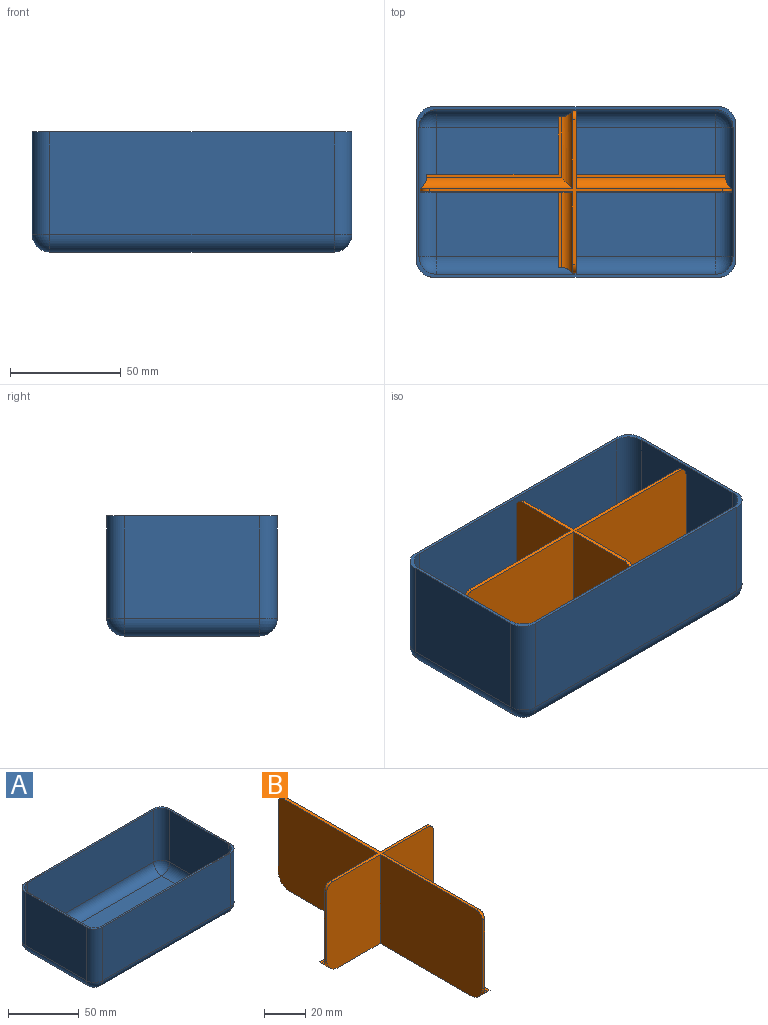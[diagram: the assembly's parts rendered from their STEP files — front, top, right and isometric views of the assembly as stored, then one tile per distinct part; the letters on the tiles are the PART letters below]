
ASSEMBLY  parts=2 mates=1
PART A: 35 faces, bbox 144.6x77.1x54.3 mm
  f0: plane 61.1x46.3mm, normal (1,0,0), area 2828.9mm2, adj f8,f13,f16,f26
  f1: plane 128.6x46.3mm, normal (0,1,0), area 5954.2mm2, adj f8,f13,f14,f22
  f2: plane 61.1x46.3mm, normal (-1,0,0), area 2828.9mm2, adj f8,f14,f15,f19
  f3: plane 58.5x45mm, normal (1,0,0), area 2632.5mm2, adj f8,f9,f12,f32
  f4: plane 126x45mm, normal (0,-1,0), area 5670mm2, adj f8,f9,f10,f28
  f5: plane 58.5x45mm, normal (-1,0,0), area 2632.5mm2, adj f8,f10,f11,f29
  f6: plane 126x45mm, normal (0,1,0), area 5670mm2, adj f8,f11,f12,f33
  f7: plane 128.6x46.3mm, normal (0,-1,0), area 5954.2mm2, adj f8,f15,f16,f23
  f8: plane 144.6x77.1mm, normal (0,0,1), area 569.7mm2, adj f0,f1,f2,f3,f4,f5,f6,f7
  f9: cylinder r=8mm len=45mm, axis (0,0,-1), area 565.5mm2, adj f3,f4,f8,f30
  f10: cylinder r=8mm len=45mm, axis (0,0,1), area 565.5mm2, adj f4,f5,f8,f27
  f11: cylinder r=8mm len=45mm, axis (0,0,-1), area 565.5mm2, adj f5,f6,f8,f31
  f12: cylinder r=8mm len=45mm, axis (0,0,1), area 565.5mm2, adj f3,f6,f8,f34
  f13: cylinder r=8mm len=46.3mm, axis (0,0,-1), area 581.8mm2, adj f0,f1,f8,f24
  f14: cylinder r=8mm len=46.3mm, axis (0,0,1), area 581.8mm2, adj f1,f2,f8,f20
  f15: cylinder r=8mm len=46.3mm, axis (0,0,-1), area 581.8mm2, adj f2,f7,f8,f21
  f16: cylinder r=8mm len=46.3mm, axis (0,0,1), area 581.8mm2, adj f0,f7,f8,f25
  f17: plane 126x58.5mm, normal (0,0,1), area 7371mm2, adj f28,f29,f32,f33
  f18: plane 128.6x61.1mm, normal (0,0,-1), area 7857.5mm2, adj f19,f22,f23,f26
  f19: cylinder r=8mm len=61.1mm, axis (0,-1,0), area 767.8mm2, adj f2,f18,f20,f21
  f20: sphere r=8mm, area 100.5mm2, adj f14,f19,f22
  f21: sphere r=8mm, area 100.5mm2, adj f15,f19,f23
  f22: cylinder r=8mm len=128.6mm, axis (-1,0,0), area 1616mm2, adj f1,f18,f20,f24
  f23: cylinder r=8mm len=128.6mm, axis (1,0,0), area 1616mm2, adj f7,f18,f21,f25
  f24: sphere r=8mm, area 100.5mm2, adj f13,f22,f26
  f25: sphere r=8mm, area 100.5mm2, adj f16,f23,f26
  f26: cylinder r=8mm len=61.1mm, axis (0,1,0), area 767.8mm2, adj f0,f18,f24,f25
  f27: sphere r=8mm, area 100.5mm2, adj f10,f28,f29
  f28: cylinder r=8mm len=126mm, axis (1,0,0), area 1583.4mm2, adj f4,f17,f27,f30
  f29: cylinder r=8mm len=58.5mm, axis (0,-1,0), area 735.1mm2, adj f5,f17,f27,f31
  f30: sphere r=8mm, area 100.5mm2, adj f9,f28,f32
  f31: sphere r=8mm, area 100.5mm2, adj f11,f29,f33
  f32: cylinder r=8mm len=58.5mm, axis (0,1,0), area 735.1mm2, adj f3,f17,f30,f34
  f33: cylinder r=8mm len=126mm, axis (-1,0,0), area 1583.4mm2, adj f6,f17,f31,f34
  f34: sphere r=8mm, area 100.5mm2, adj f12,f32,f33
PART B: 33 faces, bbox 73.5x140.7x53 mm
  f0: plane 59.64x2mm, normal (1,0,0), area 116mm2, adj f7,f8,f17,f23
  f1: plane 67.64x2mm, normal (1,0,0), area 132mm2, adj f2,f7,f19,f24
  f2: plane 67.64x1.4mm, normal (0,0,1), area 94.7mm2, adj f1,f19,f24,f25
  f3: plane 68.75x46mm, normal (1,0,0), area 3159mm2, adj f9,f11,f18,f23,f26,f31
  f4: plane 70.35x46mm, normal (1,0,0), area 3232.6mm2, adj f9,f10,f19,f24,f25,f32
  f5: plane 68.75x53mm, normal (-1,0,0), area 3608.4mm2, adj f7,f9,f11,f13,f14,f15,f23,f28
  f6: plane 70.35x53mm, normal (-1,0,0), area 3711.4mm2, adj f7,f9,f10,f16,f24,f32
  f7: plane 124.7x57.5mm, normal (0,0,-1), area 1393.6mm2, adj f0,f1,f5,f6,f15,f16,f17,f19
  f8: plane 61.04x27.44mm, normal (0,0,1), area 121.9mm2, adj f0,f17,f22,f23,f26,f27
  f9: plane 132.7x65.5mm, normal (0,0,1), area 314.6mm2, adj f3,f4,f5,f6,f13,f16,f18,f19
  f10: plane 41x1.6mm, normal (0,-1,0), area 65.6mm2, adj f4,f6,f24,f32
  f11: plane 41x1.6mm, normal (0,1,0), area 65.6mm2, adj f3,f5,f23,f31
  f12: plane 41x1.6mm, normal (-1,0,0), area 65.6mm2, adj f13,f16,f21,f29
  f13: plane 46x36.75mm, normal (0,1,0), area 1687mm2, adj f5,f9,f12,f21,f28,f29
  f14: plane 34.04x1.4mm, normal (0,0,1), area 47.7mm2, adj f5,f15,f21,f28
  f15: plane 34.04x2mm, normal (0,1,0), area 64.8mm2, adj f5,f7,f14,f21
  f16: plane 53x36.75mm, normal (0,-1,0), area 1930.6mm2, adj f6,f7,f9,f12,f21,f29
  f17: plane 26.04x2mm, normal (0,1,0), area 48.8mm2, adj f0,f7,f8,f22
  f18: plane 46x35.15mm, normal (0,1,0), area 1613.4mm2, adj f3,f9,f20,f22,f27,f30
  f19: plane 53x35.15mm, normal (0,-1,0), area 1827.6mm2, adj f1,f2,f4,f7,f9,f20,f22,f25
  f20: plane 41x1.6mm, normal (1,0,0), area 65.6mm2, adj f18,f19,f22,f30
  f21: cylinder r=8mm len=8mm, axis (0,1,0), area 64.1mm2, adj f7,f12,f13,f14,f15,f16,f28
  f22: cylinder r=8mm len=8mm, axis (0,-1,0), area 64.1mm2, adj f7,f8,f17,f18,f19,f20,f27
  f23: cylinder r=8mm len=8mm, axis (1,0,0), area 64.1mm2, adj f0,f3,f5,f7,f8,f11,f26
  f24: cylinder r=8mm len=8mm, axis (-1,0,0), area 64.1mm2, adj f1,f2,f4,f6,f7,f10,f25
  f25: cylinder r=5mm len=70.29mm, axis (0,1,0), area 541.4mm2, adj f2,f4,f19,f24
  f26: cylinder r=5mm len=68.69mm, axis (0,1,0), area 514.6mm2, adj f3,f8,f23,f27
  f27: cylinder r=5mm len=35.09mm, axis (-1,0,0), area 250.7mm2, adj f8,f18,f22,f26
  f28: cylinder r=5mm len=36.69mm, axis (-1,0,0), area 277.5mm2, adj f5,f13,f14,f21
  f29: cylinder r=4mm len=4mm, axis (0,-1,0), area 10.1mm2, adj f9,f12,f13,f16
  f30: cylinder r=4mm len=4mm, axis (0,1,0), area 10.1mm2, adj f9,f18,f19,f20
  f31: cylinder r=4mm len=4mm, axis (-1,0,0), area 10.1mm2, adj f3,f5,f9,f11
  f32: cylinder r=4mm len=4mm, axis (1,0,0), area 10.1mm2, adj f4,f6,f9,f10
PLACE A t=(-25.77,-0.08,-3.66)mm
PLACE B rot(axis=(0,0,1),90deg) t=(-25.77,-0.08,-3.66)mm
MATE revolute B.f7 <-> A.f17  axis (0,0,1) through (-25.77,-0.08,-3.66)mm
